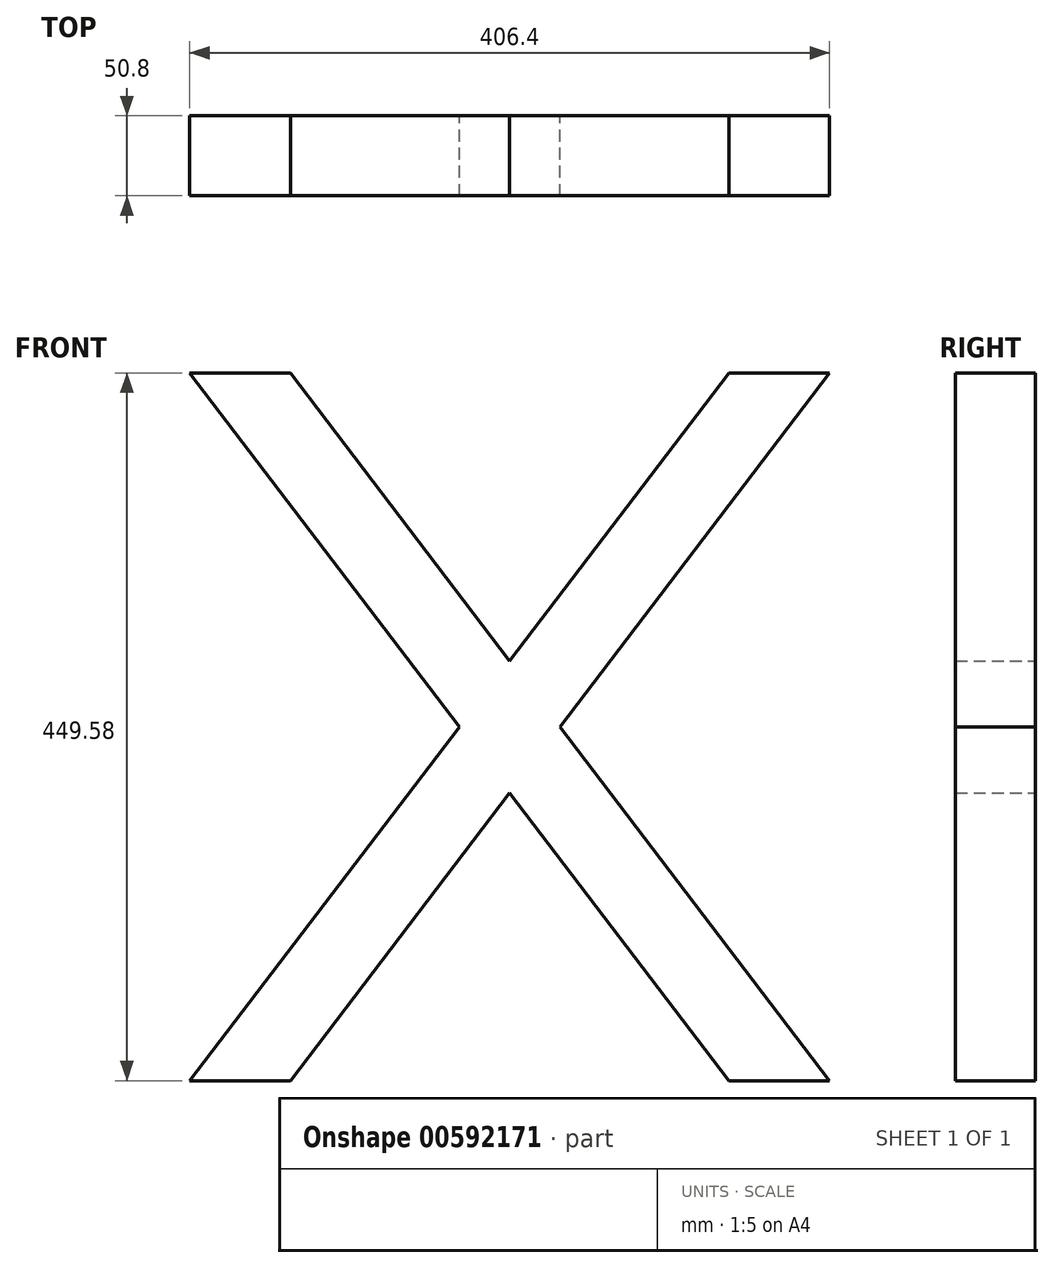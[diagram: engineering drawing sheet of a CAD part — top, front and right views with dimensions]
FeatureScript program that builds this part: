
annotation { "Feature Type Name" : "Feature", "Feature Type Description" : "" }
export const myFeature = defineFeature(function(context is Context, id is Id, definition is map)
    precondition{}
    {
        {
            var Q0;
            Q0=qCreatedBy(makeId("Front.planeOp"),FACE);
            var sketch = newSketch(context, id + "F0", { "sketchPlane" : qUnion([Q0])});
            skLineSegment(sketch, "E0.bottom", {"start": v(203.2, 224.8) * mm, "end": v(139.34, 224.8) * mm});
            skLineSegment(sketch, "E0.top", {"start": v(203.2, -224.79) * mm, "end": v(139.34, -224.79) * mm});
            skPoint(sketch, "E0.middle", {"position": v(0, 0) * mm});
            skLineSegment(sketch, "E1", {"start": v(-203.2, 224.8) * mm, "end": v(-31.93, 0) * mm});
            skLineSegment(sketch, "E2", {"start": v(139.34, -224.79) * mm, "end": v(203.2, -224.79) * mm});
            skLineSegment(sketch, "E3", {"start": v(203.2, -224.79) * mm, "end": v(31.93, 0) * mm});
            skLineSegment(sketch, "E4", {"start": v(-139.34, 224.8) * mm, "end": v(-203.2, 224.8) * mm});
            skLineSegment(sketch, "E5", {"start": v(203.2, 224.8) * mm, "end": v(31.93, 0) * mm});
            skLineSegment(sketch, "E6", {"start": v(-139.34, -224.79) * mm, "end": v(-203.2, -224.79) * mm});
            skLineSegment(sketch, "E7", {"start": v(-203.2, -224.79) * mm, "end": v(-31.93, 0) * mm});
            skLineSegment(sketch, "E8", {"start": v(139.34, 224.8) * mm, "end": v(203.2, 224.8) * mm});
            skLineSegment(sketch, "E9.trimOffspring", {"start": v(0, 41.91) * mm, "end": v(-139.34, 224.79) * mm});
            skLineSegment(sketch, "E10.trimOffspring", {"start": v(0, 41.91) * mm, "end": v(139.34, 224.8) * mm});
            skLineSegment(sketch, "E11.trimOffspring", {"start": v(0, -41.91) * mm, "end": v(139.34, -224.8) * mm});
            skLineSegment(sketch, "E12.trimOffspring", {"start": v(0, -41.91) * mm, "end": v(-139.34, -224.8) * mm});
            skSolve(sketch);
        }
        {
            var Q0;
            Q0 = qSketchRegion(id + "F0", true);
            extrude(context, id + "F1", {"entities" : qUnion([Q0]), "depth" : 50.8 * mm, "offsetDistance" : 25.4 * mm});
        }
    });
